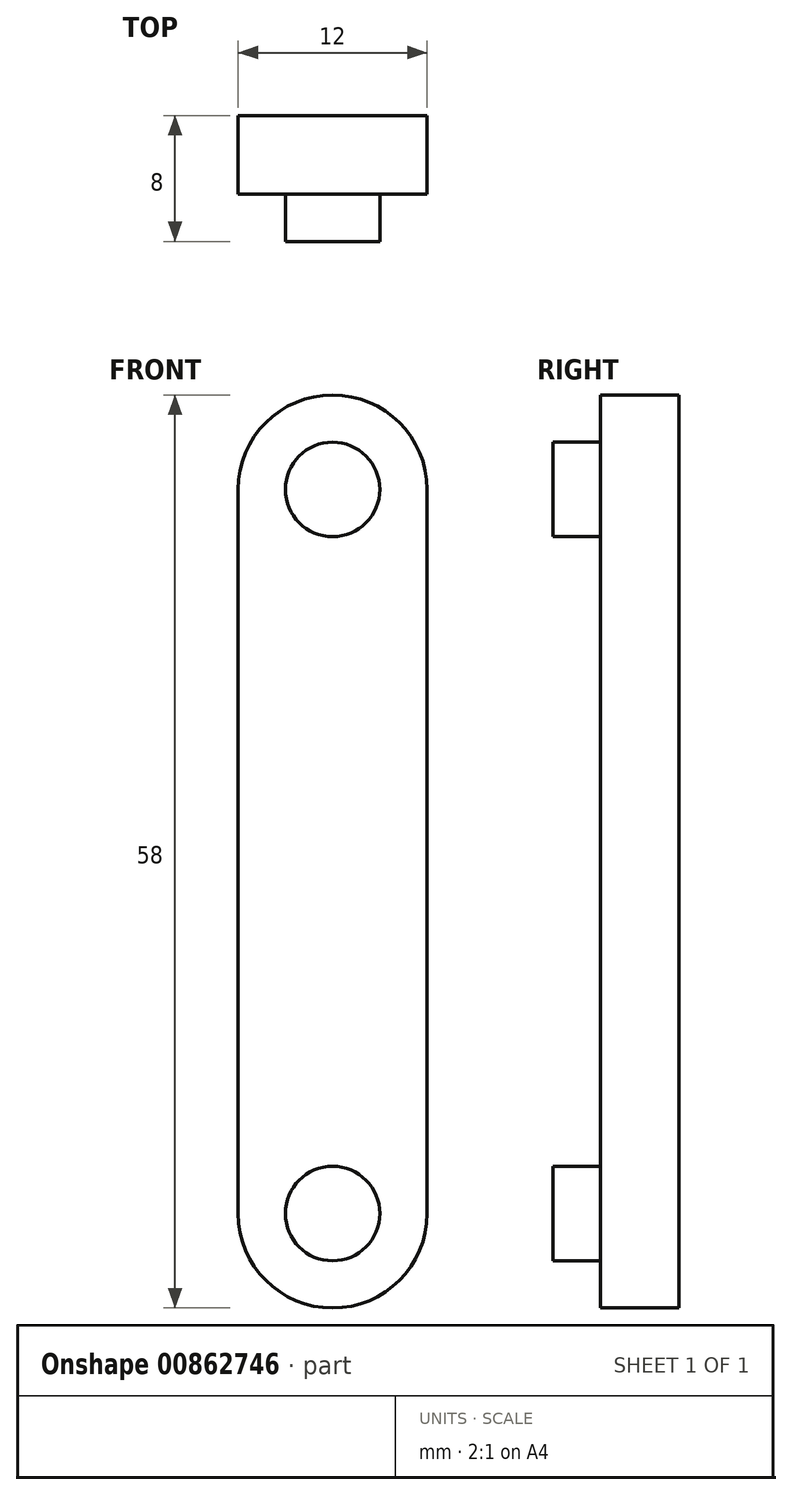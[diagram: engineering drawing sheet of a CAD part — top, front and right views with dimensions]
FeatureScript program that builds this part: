
annotation { "Feature Type Name" : "Feature", "Feature Type Description" : "" }
export const myFeature = defineFeature(function(context is Context, id is Id, definition is map)
    precondition{}
    {
        {
            var Q0;
            Q0=qCreatedBy(makeId("Front.planeOp"),FACE);
            var sketch = newSketch(context, id + "F0", { "sketchPlane" : qUnion([Q0])});
            skLineSegment(sketch, "E0", {"start": v(0, 0) * mm, "end": v(0, 46) * mm});
            skArc(sketch, "E1", {"start": v(12, 46) * mm, "mid": v(6, 52) * mm, "end": v(0, 46) * mm});
            skLineSegment(sketch, "E2", {"start": v(12, 46) * mm, "end": v(12, 0) * mm});
            skArc(sketch, "E3", {"start": v(0, 0) * mm, "mid": v(6, -6) * mm, "end": v(12, 0) * mm});
            skSolve(sketch);
        }
        {
            var Q0;
            Q0=makeQuery(id+"F0.imprint","IMPRINT",FACE,{"disambiguationData":[TD([[makeQuery(id+"F0.imprint","IMPRINT",EDGE,{"derivedFrom":sQuery(id+"F0.wireOp",EDGE,"E0")}),-1.0]])]});
            extrude(context, id + "F1", {"entities" : qUnion([Q0]), "depth" : 5 * mm, "offsetDistance" : 25 * mm});
        }
        {
            var Q0;
            Q0=makeQuery(id+"F1.opExtrude","CAP_FACE",FACE,{"disambiguationData":[OSD([sQuery(id+"F0.wireOp",EDGE,"E0"),sQuery(id+"F0.wireOp",EDGE,"E1"),sQuery(id+"F0.wireOp",EDGE,"E2"),sQuery(id+"F0.wireOp",EDGE,"E3")])],"isStart":false});
            var sketch = newSketch(context, id + "F2", { "sketchPlane" : qUnion([Q0])});
            skCircle(sketch, "E4", {"center": v(6, 0) * mm, "radius": 3 * mm});
            skCircle(sketch, "E5", {"center": v(6, 46) * mm, "radius": 3 * mm});
            skSolve(sketch);
        }
        {
            var Q0;
            Q0=makeQuery(id+"F2.imprint","IMPRINT",FACE,{"disambiguationData":[TD([[makeQuery(id+"F2.imprint","IMPRINT",EDGE,{"derivedFrom":sQuery(id+"F2.wireOp",EDGE,"E5")}),1.0]])]});
            var Q1;
            Q1=makeQuery(id+"F2.imprint","IMPRINT",FACE,{"disambiguationData":[TD([[makeQuery(id+"F2.imprint","IMPRINT",EDGE,{"derivedFrom":sQuery(id+"F2.wireOp",EDGE,"E4")}),1.0]])]});
            extrude(context, id + "F3", {"entities" : qUnion([Q0, Q1]), "operationType" : NewBodyOperationType.ADD, "depth" : 3 * mm, "offsetDistance" : 25 * mm});
        }
    });
